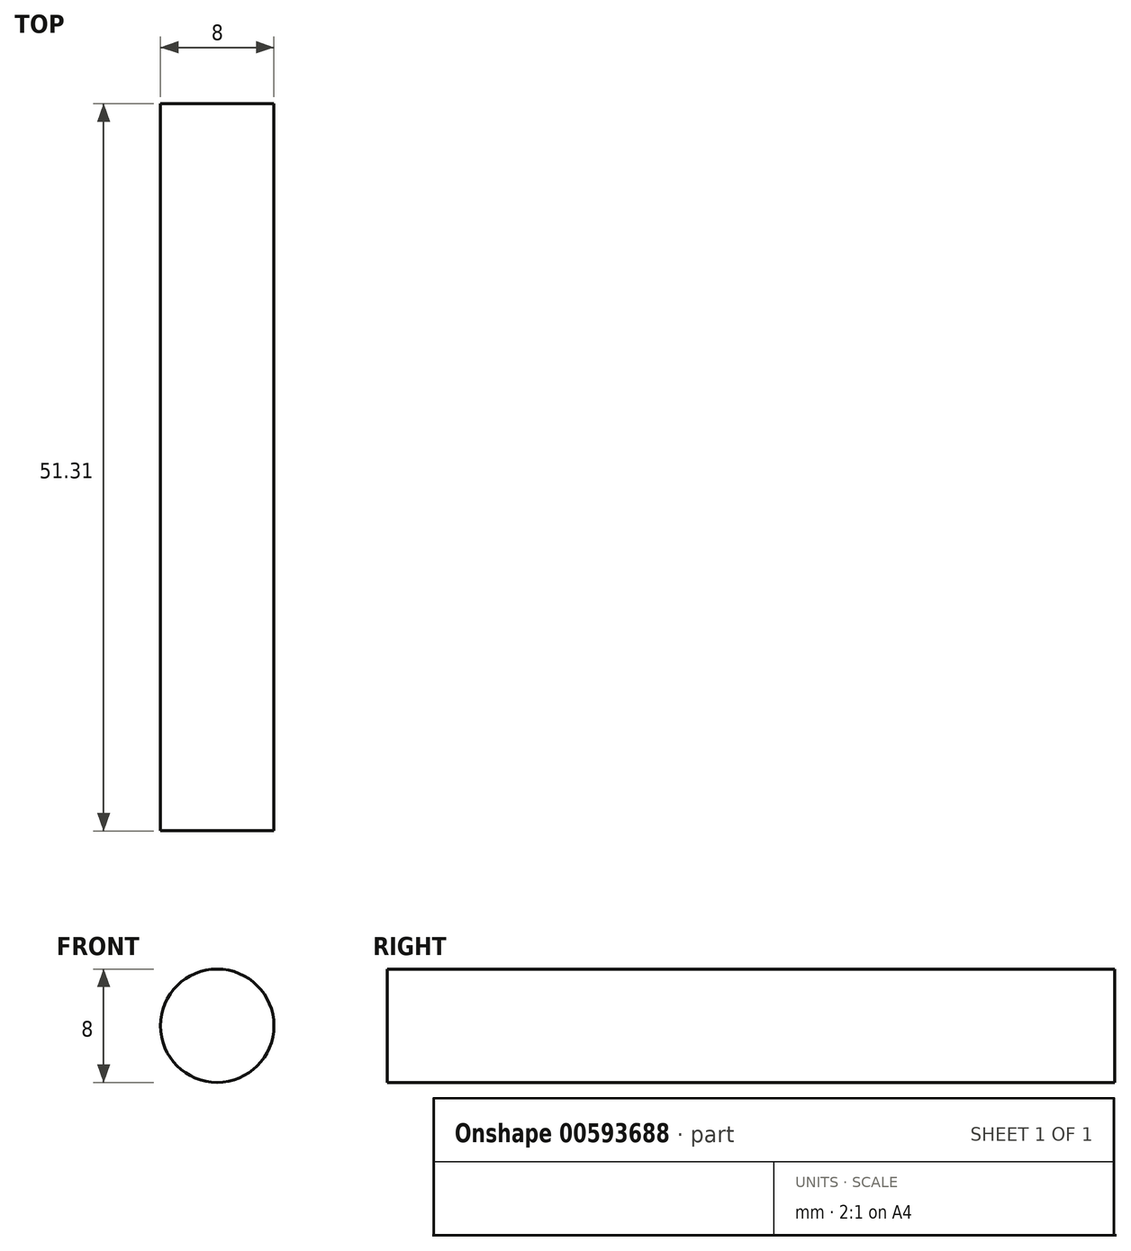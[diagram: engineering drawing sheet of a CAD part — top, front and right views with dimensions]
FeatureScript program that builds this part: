
annotation { "Feature Type Name" : "Feature", "Feature Type Description" : "" }
export const myFeature = defineFeature(function(context is Context, id is Id, definition is map)
    precondition{}
    {
        {
            var Q0;
            Q0=qCreatedBy(makeId("Front.planeOp"),FACE);
            var sketch = newSketch(context, id + "F0", { "sketchPlane" : qUnion([Q0])});
            skCircle(sketch, "E0", {"center": v(0, 0) * mm, "radius": 4 * mm});
            skSolve(sketch);
        }
        {
            var Q0;
            Q0 = qSketchRegion(id + "F0", true);
            extrude(context, id + "F1", {"entities" : qUnion([Q0]), "depth" : 51.3 * mm, "offsetDistance" : 25.4 * mm});
        }
    });
